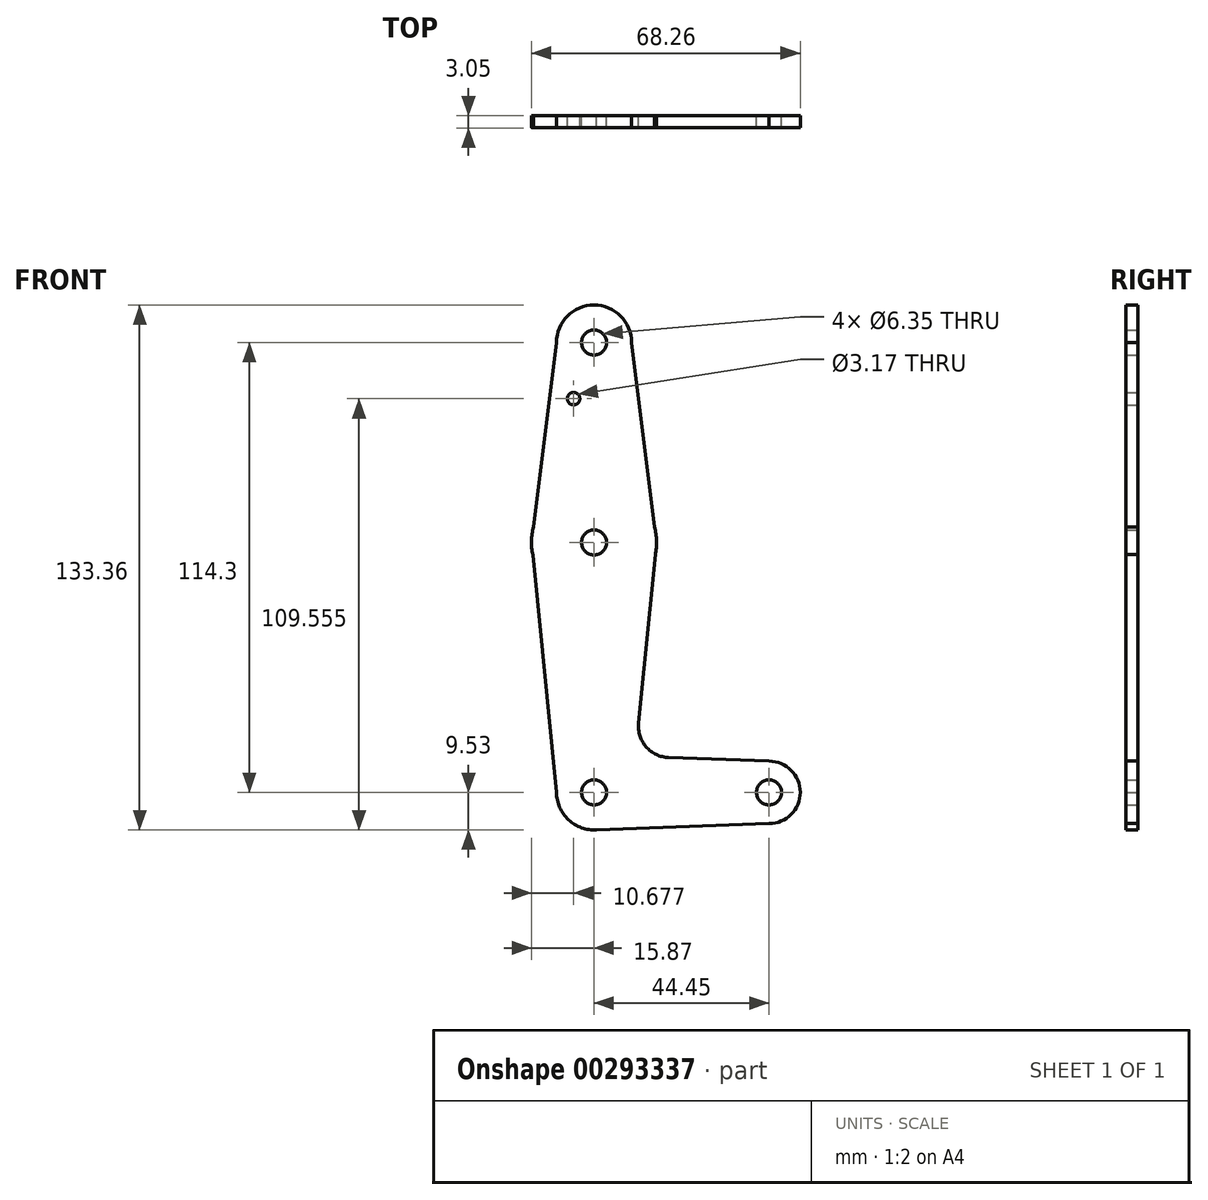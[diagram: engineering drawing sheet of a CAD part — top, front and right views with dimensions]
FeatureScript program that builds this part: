
annotation { "Feature Type Name" : "Feature", "Feature Type Description" : "" }
export const myFeature = defineFeature(function(context is Context, id is Id, definition is map)
    precondition{}
    {
        {
            var Q0;
            Q0=qCreatedBy(makeId("Front.planeOp"),FACE);
            var sketch = newSketch(context, id + "F0", { "sketchPlane" : qUnion([Q0])});
            skCircle(sketch, "E0", {"center": v(0, 114.3) * mm, "radius": 9.53 * mm});
            skLineSegment(sketch, "E1", {"start": v(0, 114.3) * mm, "end": v(0, 0) * mm});
            skLineSegment(sketch, "E2", {"start": v(0, 0) * mm, "end": v(44.45, 0) * mm});
            skCircle(sketch, "E3", {"center": v(0, 63.5) * mm, "radius": 15.88 * mm});
            skCircle(sketch, "E4", {"center": v(0, 0) * mm, "radius": 9.53 * mm});
            skCircle(sketch, "E5", {"center": v(44.45, 0) * mm, "radius": 7.94 * mm});
            skLineSegment(sketch, "E6", {"start": v(9.52, 114.3) * mm, "end": v(15.88, 63.5) * mm});
            skLineSegment(sketch, "E7", {"start": v(15.88, 63.5) * mm, "end": v(11.32, 17.58) * mm});
            skLineSegment(sketch, "E8", {"start": v(18.94, 8.85) * mm, "end": v(44.45, 7.94) * mm});
            skLineSegment(sketch, "E9", {"start": v(0, -9.53) * mm, "end": v(44.45, -7.94) * mm});
            skCircle(sketch, "E10", {"center": v(0, 114.3) * mm, "radius": 3.18 * mm});
            skCircle(sketch, "E11", {"center": v(0, 63.5) * mm, "radius": 3.18 * mm});
            skCircle(sketch, "E12", {"center": v(0, 0) * mm, "radius": 3.18 * mm});
            skCircle(sketch, "E13", {"center": v(44.45, 0) * mm, "radius": 3.18 * mm});
            skLineSegment(sketch, "E14.filletArc", {"start": v(0, 0) * mm, "end": v(0, 0) * mm});
            skPoint(sketch, "E15.visualSharp", {"position": v(9.57, 0) * mm});
            skArc(sketch, "E16.filletArc", {"start": v(11.32, 17.58) * mm, "mid": v(13.24, 11.56) * mm, "end": v(18.94, 8.85) * mm});
            skCircle(sketch, "E17", {"center": v(-5.2, 100.03) * mm, "radius": 1.59 * mm});
            skLineSegment(sketch, "E18", {"start": v(-15.87, 63.5) * mm, "end": v(-9.53, 0) * mm});
            skLineSegment(sketch, "E19", {"start": v(-9.53, 114.3) * mm, "end": v(-15.88, 63.5) * mm});
            skSolve(sketch);
        }
        {
            var Q0;
            Q0 = qSketchRegion(id + "F0", true);
            var Q1;
            {var subQ0=sQuery(id+"F0.wireOp",EDGE,"E4");var subQ1=sQuery(id+"F0.wireOp",EDGE,"E1");var subQ2=makeQuery(id+"F0.imprint","INTERSECT",VERTEX,{"derivedFrom":[subQ1,subQ0]});Q1=makeQuery(id+"F0.imprint","IMPRINT",FACE,{"disambiguationData":[TD([[makeQuery(id+"F0.imprint","IMPRINT",EDGE,{"disambiguationData":[TD([[subQ2,-1.0]])],"derivedFrom":subQ1}),1.0]])]});}
            extrude(context, id + "F1", {"entities" : qUnion([Q0, Q1]), "depth" : 3.05 * mm});
        }
    });
